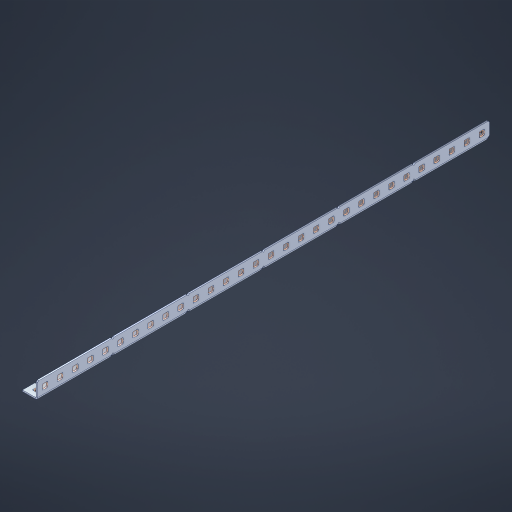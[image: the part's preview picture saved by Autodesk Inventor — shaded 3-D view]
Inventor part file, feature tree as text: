
AUTODESK INVENTOR PART (.ipt)
format: ipt  version: 2023 (Build 270158000, 158)  size: 1,218,560 bytes
history: native  units: in
note: dims shown in document units (in); Inventor stores cm internally (conversion verified against a paired STEP export)
features: other x97, extrude x88, sheet_metal_op x11, sketch x10, pattern_linear x2, mirror x1, chamfer x1
ambient origin geometry x8: Origin, YZ Plane, XZ Plane, XY Plane, X Axis, Y Axis, Z Axis, Center Point
bodies: Solid1 (feature_tree), Body (feature_tree)
feature tree (210):
  sheet_metal_op  "Flanges"
  other  "Flange Pattern Plane"
  other  "Flange Pattern Sketch"
  sheet_metal_op  "Flange Pattern"
  sheet_metal_op  "Body Pattern"
  pattern_linear  "Center Pattern"  Spacing1=0.0469in  [1 undecoded]
  other  "Arc Length"
  mirror  "Notch Mirror"
  pattern_linear  "Notch Pattern"  Spacing1=0.182in  [1 undecoded]
  chamfer  "End Chamfer"
  extrude  "Half Cut"  Depth=0.02in
  sketch  "Sketch1"  dims[d0=1.0in]
  other  "Plate1"
  sketch  "Sketch2"  dims[d1=15.0in]
  other  "Plate2"
  sheet_metal_op  "Bend1"
  sheet_metal_op  "Corner1"
  sketch  "Sketch3"  dims[d2=0.0469in]
  sketch  "Sketch7"  dims[d3=0.0469in]
  other  "Srf1"
  other  "Srf2"
  sketch  "Sketch8"  dims[d4=0.0234in]
  sketch  "Sketch9"  dims[d5=0.0938in]
  other  "Srf91"
  sheet_metal_op  "Body Pattern Sketch"
  other  "Srf92"
  sketch  "Sketch13"  dims[d6=0.0469in]
  sketch  "Sketch14"  dims[d7=0.5in d8=90.0deg d9=0.0312in]
  sketch  "Sketch15"  dims[d10=0.1875in]
  sketch  "Sketch16"  dims[d11=0.0469in d12=0.0469in d16=0.182in d17=0.02in d18=0.0469in d19=0.0in d20=0.25in d21=0.25in d38=11.811in d40=0.5in d41=0.3937in d43=1.0in d46=0.172in d47=1.0in d48=0.0in d49=0.182in d50=0.02in d51=0.25in d52=0.25in d53=0.0469in d54=0.0in d55=0.172in d56=1.0in d57=0.0in d58=0.25in d60=11.811in d62=0.5in d63=0.3937in d65=0.5in d85=0.1227in d86=0.1659in d88=0.04in d89=0.0469in d90=0.0in d91=0.04in d92=0.0491in d95=2.5in d96=0.04in d97=0.25in d98=45.0deg d99=0.25in d100=0.5in d101=0.0in d102=2.497in d106=0.182in d107=0.02in d108=0.5in d109=0.5in d110=0.0469in d111=0.0in d112=0.172in d113=0.5in d114=0.0in d117=0.5in d118=0.5in d119=0.5in]
  other  "Srf786"
  other  "Srf823"
  other  "Srf824"
  other  "Srf825"
  other  "Srf826"
  other  "Srf827"
  other  "Srf828"
  other  "Srf829"
  other  "Srf856"
  other  "Srf857"
  other  "Srf858"
  other  "Srf859"
  other  "Srf860"
  other  "Srf861"
  other  "Srf862"
  other  "Srf889"
  other  "Srf890"
  other  "Srf891"
  other  "Srf892"
  other  "Srf893"
  other  "Srf894"
  other  "Srf895"
  other  "Srf896"
  other  "Srf922"
  other  "Srf923"
  other  "Srf924"
  other  "Srf925"
  other  "Srf926"
  other  "Srf959"
  other  "Srf960"
  other  "Srf961"
  other  "Srf962"
  other  "Srf963"
  other  "Srf996"
  other  "Srf997"
  other  "Srf998"
  other  "Srf999"
  other  "Srf1000"
  other  "Srf1143"
  other  "Srf1144"
  other  "Srf1145"
  other  "Srf1146"
  other  "Srf1147"
  other  "Srf1148"
  other  "Srf1149"
  other  "Srf1150"
  other  "Srf1151"
  other  "Srf1152"
  other  "Srf1153"
  other  "Srf1154"
  other  "Srf1155"
  other  "Srf1156"
  other  "Srf1157"
  other  "Srf1158"
  other  "Srf1199"
  other  "Srf1200"
  other  "Srf1201"
  other  "Srf1202"
  other  "Srf1203"
  other  "Srf1204"
  other  "Srf1205"
  other  "Srf1206"
  other  "Srf1207"
  other  "Srf1208"
  other  "Srf1209"
  other  "Srf1210"
  other  "Srf1211"
  other  "Srf1212"
  other  "Srf1213"
  other  "Srf1214"
  other  "Srf1255"
  other  "Srf1256"
  other  "Srf1257"
  other  "Srf1258"
  other  "Srf1259"
  other  "Srf1260"
  other  "Srf1261"
  other  "Srf1262"
  other  "Srf1263"
  other  "Srf1264"
  other  "Srf1265"
  other  "Srf1266"
  other  "Srf1267"
  other  "Srf1268"
  other  "Srf1269"
  other  "Srf1270"
  sheet_metal_op  "Flange Stamp"
  sheet_metal_op  "Flange Circle"
  sheet_metal_op  "Body Stamp"
  sheet_metal_op  "Body Circle"
  other  "Center Stamp"
  other  "Center Circle"
  sheet_metal_op  "Notch"
  extrude  "ExtrusionSrf2"  Depth=0.0469in
  extrude  "ExtrusionSrf92"  TaperAngle=0.0deg  [1 undecoded]
  extrude  "ExtrusionSrf823"  Depth=0.25in
  extrude  "ExtrusionSrf824"  Depth=0.25in
  extrude  "ExtrusionSrf825"  Depth=0.5in
  extrude  "ExtrusionSrf826"  Depth=0.5in
  extrude  "ExtrusionSrf827"  Depth=1.0in TaperAngle=0.0deg
  extrude  "ExtrusionSrf828"  Depth=0.182in
  extrude  "ExtrusionSrf829"  Depth=0.02in
  extrude  "ExtrusionSrf856"  Depth=0.25in
  extrude  "ExtrusionSrf857"  Depth=0.25in
  extrude  "ExtrusionSrf858"  Depth=0.0469in
  extrude  "ExtrusionSrf859"  TaperAngle=0.0deg  [1 undecoded]
  extrude  "ExtrusionSrf860"  Depth=0.5in
  extrude  "ExtrusionSrf861"  Depth=1.0in TaperAngle=0.0deg
  extrude  "ExtrusionSrf862"  Depth=0.25in
  extrude  "ExtrusionSrf889"  Depth=0.5in
  extrude  "ExtrusionSrf890"  Depth=0.5in
  extrude  "ExtrusionSrf891"  Depth=0.5in
  extrude  "ExtrusionSrf892"  Depth=0.5in
  extrude  "ExtrusionSrf893"  Depth=0.5in
  extrude  "ExtrusionSrf894"  Depth=0.0469in
  extrude  "ExtrusionSrf895"  TaperAngle=0.0deg  [1 undecoded]
  extrude  "ExtrusionSrf896"  Depth=0.5in
  extrude  "ExtrusionSrf922"  Depth=0.5in
  extrude  "ExtrusionSrf923"  Depth=2.5in
  extrude  "ExtrusionSrf924"  Depth=0.25in TaperAngle=45.0deg
  extrude  "ExtrusionSrf925"  Depth=0.25in
  extrude  "ExtrusionSrf926"  Depth=0.5in TaperAngle=0.0deg
  extrude  "ExtrusionSrf959"  Depth=0.5in
  extrude  "ExtrusionSrf960"  Depth=0.182in
  extrude  "ExtrusionSrf961"  Depth=0.02in
  extrude  "ExtrusionSrf962"  Depth=0.5in
  extrude  "ExtrusionSrf963"  Depth=0.5in
  extrude  "ExtrusionSrf996"  Depth=0.0469in
  extrude  "ExtrusionSrf997"  TaperAngle=0.0deg  [1 undecoded]
  extrude  "ExtrusionSrf998"  Depth=0.5in
  extrude  "ExtrusionSrf999"  Depth=0.5in TaperAngle=0.0deg
  extrude  "ExtrusionSrf1000"  Depth=0.5in
  extrude  "ExtrusionSrf1143"  Depth=0.5in
  extrude  "ExtrusionSrf1144"  Depth=0.5in
  extrude  "ExtrusionSrf1145"  [1 undecoded]
  extrude  "ExtrusionSrf1146"  [1 undecoded]
  extrude  "ExtrusionSrf1147"  [1 undecoded]
  extrude  "ExtrusionSrf1148"  [1 undecoded]
  extrude  "ExtrusionSrf1149"  [1 undecoded]
  extrude  "ExtrusionSrf1150"  [1 undecoded]
  extrude  "ExtrusionSrf1151"  [1 undecoded]
  extrude  "ExtrusionSrf1152"  [1 undecoded]
  extrude  "ExtrusionSrf1153"  [1 undecoded]
  extrude  "ExtrusionSrf1154"  [1 undecoded]
  extrude  "ExtrusionSrf1155"  [1 undecoded]
  extrude  "ExtrusionSrf1156"  [1 undecoded]
  extrude  "ExtrusionSrf1157"  [1 undecoded]
  extrude  "ExtrusionSrf1158"  [1 undecoded]
  extrude  "ExtrusionSrf1199"  [1 undecoded]
  extrude  "ExtrusionSrf1200"  [1 undecoded]
  extrude  "ExtrusionSrf1201"  [1 undecoded]
  extrude  "ExtrusionSrf1202"  [1 undecoded]
  extrude  "ExtrusionSrf1203"  [1 undecoded]
  extrude  "ExtrusionSrf1204"  [1 undecoded]
  extrude  "ExtrusionSrf1205"  [1 undecoded]
  extrude  "ExtrusionSrf1206"  [1 undecoded]
  extrude  "ExtrusionSrf1207"  [1 undecoded]
  extrude  "ExtrusionSrf1208"  [1 undecoded]
  extrude  "ExtrusionSrf1209"  [1 undecoded]
  extrude  "ExtrusionSrf1210"  [1 undecoded]
  extrude  "ExtrusionSrf1211"  [1 undecoded]
  extrude  "ExtrusionSrf1212"  [1 undecoded]
  extrude  "ExtrusionSrf1213"  [1 undecoded]
  extrude  "ExtrusionSrf1214"  [1 undecoded]
  extrude  "ExtrusionSrf1255"  [1 undecoded]
  extrude  "ExtrusionSrf1256"  [1 undecoded]
  extrude  "ExtrusionSrf1257"  [1 undecoded]
  extrude  "ExtrusionSrf1258"  [1 undecoded]
  extrude  "ExtrusionSrf1259"  [1 undecoded]
  extrude  "ExtrusionSrf1260"  [1 undecoded]
  extrude  "ExtrusionSrf1261"  [1 undecoded]
  extrude  "ExtrusionSrf1262"  [1 undecoded]
  extrude  "ExtrusionSrf1263"  [1 undecoded]
  extrude  "ExtrusionSrf1264"  [1 undecoded]
  extrude  "ExtrusionSrf1265"  [1 undecoded]
  extrude  "ExtrusionSrf1266"  [1 undecoded]
  extrude  "ExtrusionSrf1267"  [1 undecoded]
  extrude  "ExtrusionSrf1268"  [1 undecoded]
  extrude  "ExtrusionSrf1269"  [1 undecoded]
  extrude  "ExtrusionSrf1270"  [1 undecoded]
note: 52 required parameter values undecoded (feature->parameter linkage not recoverable at this tier; creation-order binding heuristic only, values carry confidence <= 0.55)
